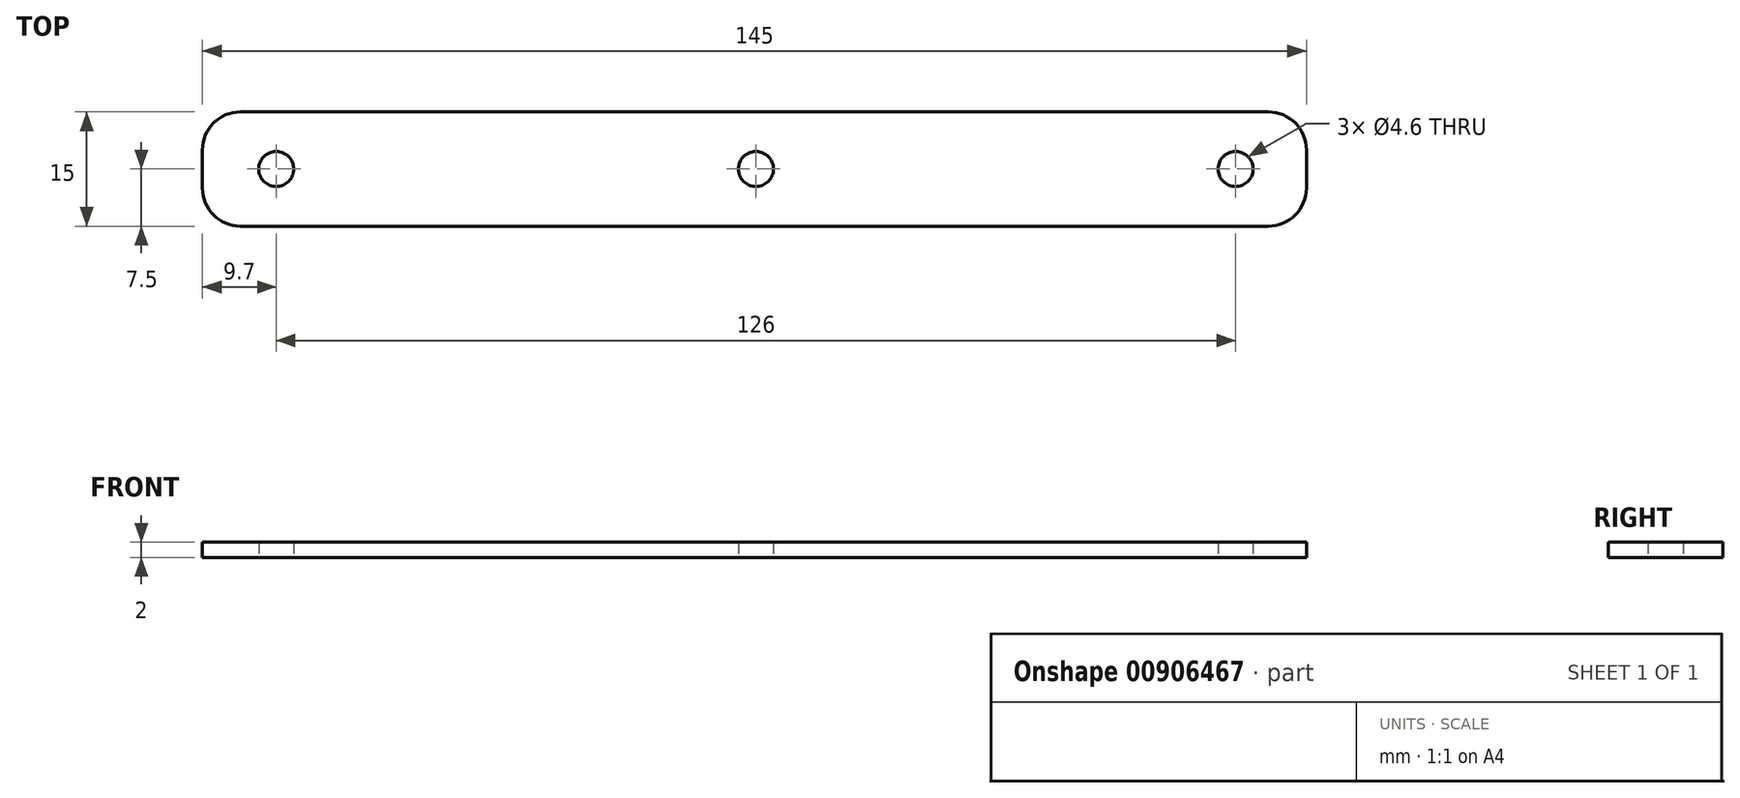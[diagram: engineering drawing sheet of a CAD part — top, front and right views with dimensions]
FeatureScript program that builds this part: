
annotation { "Feature Type Name" : "Feature", "Feature Type Description" : "" }
export const myFeature = defineFeature(function(context is Context, id is Id, definition is map)
    precondition{}
    {
        {
            var Q0;
            Q0=qCreatedBy(makeId("Top.planeOp"),FACE);
            var Q1;
            Q1=qCreatedBy(makeId("Top.planeOp"),FACE);
            var Q2;
            Q2=qCreatedBy(makeId("Top.planeOp"),FACE);
            var sketch = newSketch(context, id + "F0", { "sketchPlane" : qUnion([Q0, Q1, Q2])});
            skLineSegment(sketch, "E0", {"start": v(-67.5, 0) * mm, "end": v(67.5, 0) * mm});
            skLineSegment(sketch, "E1", {"start": v(-72.5, -5) * mm, "end": v(-72.5, -10) * mm});
            skLineSegment(sketch, "E2", {"start": v(72.5, -5) * mm, "end": v(72.5, -10) * mm});
            skLineSegment(sketch, "E3", {"start": v(67.5, -15) * mm, "end": v(-67.5, -15) * mm});
            skPoint(sketch, "E4.visualSharp", {"position": v(-72.5, 0) * mm});
            skArc(sketch, "E4.filletArc", {"start": v(-67.5, 0) * mm, "mid": v(-71.04, -1.46) * mm, "end": v(-72.5, -5) * mm});
            skPoint(sketch, "E5.visualSharp", {"position": v(-72.5, -15) * mm});
            skArc(sketch, "E5.filletArc", {"start": v(-72.5, -10) * mm, "mid": v(-71.04, -13.54) * mm, "end": v(-67.5, -15) * mm});
            skPoint(sketch, "E6.visualSharp", {"position": v(72.5, 0) * mm});
            skArc(sketch, "E6.filletArc", {"start": v(72.5, -5) * mm, "mid": v(71.04, -1.46) * mm, "end": v(67.5, 0) * mm});
            skPoint(sketch, "E7.visualSharp", {"position": v(72.5, -15) * mm});
            skArc(sketch, "E7.filletArc", {"start": v(67.5, -15) * mm, "mid": v(71.04, -13.54) * mm, "end": v(72.5, -10) * mm});
            skSolve(sketch);
        }
        {
            var Q0;
            Q0=makeQuery(id+"F0.imprint","IMPRINT",FACE,{"disambiguationData":[TD([[makeQuery(id+"F0.imprint","IMPRINT",EDGE,{"derivedFrom":sQuery(id+"F0.wireOp",EDGE,"E0")}),-1.0]])]});
            extrude(context, id + "F1", {"entities" : qUnion([Q0]), "depth" : 2 * mm, "offsetDistance" : 25 * mm});
        }
        {
            var Q0;
            Q0=makeQuery(id+"F1.opExtrude","CAP_FACE",FACE,{"disambiguationData":[OSD([sQuery(id+"F0.wireOp",EDGE,"E0"),sQuery(id+"F0.wireOp",EDGE,"E1"),sQuery(id+"F0.wireOp",EDGE,"E2"),sQuery(id+"F0.wireOp",EDGE,"E3"),sQuery(id+"F0.wireOp",EDGE,"E4.filletArc"),sQuery(id+"F0.wireOp",EDGE,"E5.filletArc"),sQuery(id+"F0.wireOp",EDGE,"E6.filletArc"),sQuery(id+"F0.wireOp",EDGE,"E7.filletArc")])],"isStart":false});
            var Q1;
            Q1=makeQuery(id+"F1.opExtrude","CAP_FACE",FACE,{"disambiguationData":[OSD([sQuery(id+"F0.wireOp",EDGE,"E0"),sQuery(id+"F0.wireOp",EDGE,"E1"),sQuery(id+"F0.wireOp",EDGE,"E2"),sQuery(id+"F0.wireOp",EDGE,"E3"),sQuery(id+"F0.wireOp",EDGE,"E4.filletArc"),sQuery(id+"F0.wireOp",EDGE,"E5.filletArc"),sQuery(id+"F0.wireOp",EDGE,"E6.filletArc"),sQuery(id+"F0.wireOp",EDGE,"E7.filletArc")])],"isStart":false});
            var sketch = newSketch(context, id + "F2", { "sketchPlane" : qUnion([Q0, Q1])});
            skPoint(sketch, "E8", {"position": v(-72.5, -7.5) * mm});
            skLineSegment(sketch, "E9", {"start": v(-72.5, -7.5) * mm, "end": v(-62.8, -7.5) * mm});
            skCircle(sketch, "E10", {"center": v(-62.8, -7.5) * mm, "radius": 2.3 * mm});
            skLineSegment(sketch, "E11", {"start": v(-62.8, -7.5) * mm, "end": v(0.2, -7.5) * mm});
            skCircle(sketch, "E12", {"center": v(0.2, -7.5) * mm, "radius": 2.3 * mm});
            skLineSegment(sketch, "E13", {"start": v(0.2, -7.5) * mm, "end": v(63.2, -7.5) * mm});
            skCircle(sketch, "E14", {"center": v(63.2, -7.5) * mm, "radius": 2.3 * mm});
            skSolve(sketch);
        }
        {
            var Q0;
            {var subQ0=sQuery(id+"F2.wireOp",EDGE,"E11");var subQ1=sQuery(id+"F2.wireOp",EDGE,"E9");var subQ2=makeQuery(id+"F2.imprint","INTERSECT",VERTEX,{"derivedFrom":[subQ1,subQ0]});Q0=makeQuery(id+"F2.imprint","IMPRINT",FACE,{"disambiguationData":[TD([[makeQuery(id+"F2.imprint","IMPRINT",EDGE,{"disambiguationData":[TD([[subQ2,1.0]])],"derivedFrom":subQ1}),-1.0]])]});}
            var Q1;
            {var subQ0=sQuery(id+"F2.wireOp",EDGE,"E11");var subQ1=sQuery(id+"F2.wireOp",EDGE,"E9");var subQ2=makeQuery(id+"F2.imprint","INTERSECT",VERTEX,{"derivedFrom":[subQ1,subQ0]});Q1=makeQuery(id+"F2.imprint","IMPRINT",FACE,{"disambiguationData":[TD([[makeQuery(id+"F2.imprint","IMPRINT",EDGE,{"disambiguationData":[TD([[subQ2,1.0]])],"derivedFrom":subQ1}),1.0]])]});}
            var Q2;
            {var subQ0=sQuery(id+"F2.wireOp",EDGE,"E13");var subQ1=sQuery(id+"F2.wireOp",EDGE,"E11");var subQ2=makeQuery(id+"F2.imprint","INTERSECT",VERTEX,{"derivedFrom":[subQ1,subQ0]});Q2=makeQuery(id+"F2.imprint","IMPRINT",FACE,{"disambiguationData":[TD([[makeQuery(id+"F2.imprint","IMPRINT",EDGE,{"disambiguationData":[TD([[subQ2,1.0]])],"derivedFrom":subQ1}),1.0]])]});}
            var Q3;
            {var subQ0=sQuery(id+"F2.wireOp",EDGE,"E13");var subQ1=sQuery(id+"F2.wireOp",EDGE,"E11");var subQ2=makeQuery(id+"F2.imprint","INTERSECT",VERTEX,{"derivedFrom":[subQ1,subQ0]});Q3=makeQuery(id+"F2.imprint","IMPRINT",FACE,{"disambiguationData":[TD([[makeQuery(id+"F2.imprint","IMPRINT",EDGE,{"disambiguationData":[TD([[subQ2,1.0]])],"derivedFrom":subQ1}),-1.0]])]});}
            var Q4;
            Q4=makeQuery(id+"F2.imprint","IMPRINT",FACE,{"disambiguationData":[TD([[makeQuery(id+"F2.imprint","IMPRINT",EDGE,{"derivedFrom":sQuery(id+"F2.wireOp",EDGE,"E14")}),1.0]])]});
            var Q5;
            Q5=sQuery(id+"F2.wireOp",EDGE,"E10");
            var Q6;
            Q6=sQuery(id+"F2.wireOp",EDGE,"E12");
            var Q7;
            Q7=sQuery(id+"F2.wireOp",EDGE,"E14");
            extrude(context, id + "F3", {"entities" : qUnion([Q0, Q1, Q2, Q3, Q4]), "operationType" : NewBodyOperationType.REMOVE, "surfaceEntities" : qUnion([Q5, Q6, Q7]), "endBound" : BoundingType.SYMMETRIC, "depth" : 25 * mm, "offsetDistance" : 25 * mm});
        }
    });
